# Revit family: F35-BLADE ZERO DEGREE
name_source: partatom
category: Air Terminals
revit_build: Autodesk Revit 2018 (Build: 20170223_1515(x64)
units: mm (PartAtom-declared; Revit-internal decimal feet)

## family parameters
Always vertical = Yes
Cut with Voids When Loaded = No
OmniClass Number = 23.75.00.00
OmniClass Title = Climate Control (HVAC)
Part Type = Normal
Room Calculation Point = No
Round Connector Dimension = Use Diameter
Shared = No
Work Plane-Based = No

## types (12) — shared parameters
BladeAngle = 138.00°
BladeHi = 0' - 0 3/4"
BladeSpacing = 0' - 0 1/2"
BladeThickness = 0' - 0 1/32"
BladeWid = 0' - 0 7/16"
Bladedepth = 0' - 0 3/8"
Bladethick = 0' - 0 1/8"
Faceflange = 0' - 1 1/4"
Facethickness = 0' - 0 1/32"
Flatflange = 0' - 1"
Manufacturer = ANEMOSTAT PRODUCTS
Max Size = 4' - 0"
Min Size = 0' - 6"
Model = F35 (Surface Mounted)
URL = https://www.anemostat-hvac.com

## per-type parameters (varying)
| type | BladeHead | Description | Filter |
| F35/1/H/L | 0' - 0 3/32" | Hinged Return Filter Grille; 45 degree Deflection; 1/2" Spacing | 0' - 1 31/32" |
| F35/2/H/L | 0' - 0 3/32" | Hinged Return Filter Grille; 45 degree Deflection; 1/2" Spacing | 0' - 2 31/32" |
| F35/2S/H/L | 0' - 0 3/16" | Hinged Return Filter Grille; Zero degree Deflection; 1/2" Spacing | 0' - 2 31/32" |
| F35/2L/H/L | 0' - 0 3/32" | Hinged Return Filter Grille; 45 degree Deflection; 1/2" Spacing | 0' - 2 31/32" |
| F35/2/H/S | 0' - 0 3/32" | Hinged Return Filter Grille; 45 degree Deflection; 1/2" Spacing | 0' - 2 31/32" |
| F35/2S/H/S | 0' - 0 3/32" | Hinged Return Filter Grille; 45 degree Deflection; 1/2" Spacing | 0' - 2 31/32" |
| F35/2L/H/S | 0' - 0 3/32" | Hinged Return Filter Grille; 45 degree Deflection; 1/2" Spacing | 0' - 2 31/32" |
| F35/1S/H/L | 0' - 0 3/32" | Hinged Return Filter Grille; 45 degree Deflection; 1/2" Spacing | 0' - 1 31/32" |
| F35/1L/H/L | 0' - 0 3/32" | Hinged Return Filter Grille; 45 degree Deflection; 1/2" Spacing | 0' - 1 31/32" |
| F35/1S/H/S | 0' - 0 3/32" | Hinged Return Filter Grille; 45 degree Deflection; 1/2" Spacing | 0' - 1 31/32" |
| F35/1L/H/S | 0' - 0 3/32" | Hinged Return Filter Grille; 45 degree Deflection; 1/2" Spacing | 0' - 1 31/32" |
| F35/1/H/S | 0' - 0 3/32" | Hinged Return Filter Grille; 45 degree Deflection; 1/2" Spacing | 0' - 1 31/32" |

## geometry (parser evidence)
native form markers: Sweep x2
no freeform markers — native parametric forms only
